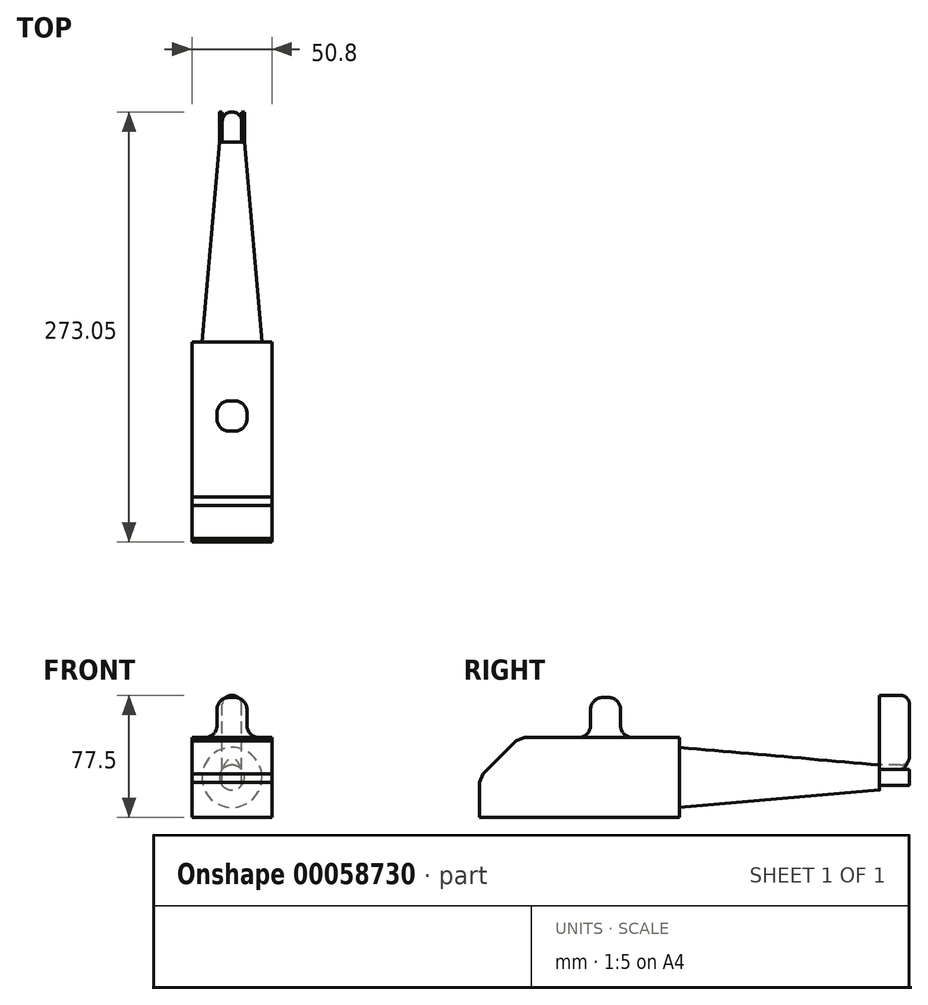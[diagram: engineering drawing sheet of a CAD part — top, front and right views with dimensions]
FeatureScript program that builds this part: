
annotation { "Feature Type Name" : "Feature", "Feature Type Description" : "" }
export const myFeature = defineFeature(function(context is Context, id is Id, definition is map)
    precondition{}
    {
        {
            var Q0;
            Q0=qCreatedBy(makeId("Top.planeOp"),FACE);
            var sketch = newSketch(context, id + "F0", { "sketchPlane" : qUnion([Q0])});
            skLineSegment(sketch, "E0.rect.bottom", {"start": v(25.4, -63.5) * mm, "end": v(-25.4, -63.5) * mm});
            skLineSegment(sketch, "E0.rect.top", {"start": v(25.4, 63.5) * mm, "end": v(-25.4, 63.5) * mm});
            skLineSegment(sketch, "E0.rect.left", {"start": v(25.4, -63.5) * mm, "end": v(25.4, 63.5) * mm});
            skLineSegment(sketch, "E0.rect.right", {"start": v(-25.4, -63.5) * mm, "end": v(-25.4, 63.5) * mm});
            skPoint(sketch, "E0.rect.middle", {"position": v(0, 0) * mm});
            skSolve(sketch);
        }
        {
            var Q0;
            Q0=makeQuery(id+"F0.imprint","IMPRINT",FACE,{"disambiguationData":[TD([[makeQuery(id+"F0.imprint","IMPRINT",EDGE,{"derivedFrom":sQuery(id+"F0.wireOp",EDGE,"E0.rect.bottom")}),-1.0]])]});
            extrude(context, id + "F1", {"entities" : qUnion([Q0]), "depth" : 50.8 * mm});
        }
        {
            var Q0;
            Q0=makeQuery(id+"F1.opExtrude","CAP_EDGE",EDGE,{"disambiguationData":[OSD([sQuery(id+"F0.wireOp",EDGE,"E0.rect.bottom")])],"isStart":false});
            chamfer(context, id + "F2", {"entities" : qUnion([Q0]), "width" : 25.4 * mm, "tangentPropagation" : true});
        }
        {
            var Q0;
            {var subQ0=sQuery(id+"F0.wireOp",EDGE,"E0.rect.bottom");Q0=makeQuery(id+"F2.opChamfer","BLEND_EDGE",EDGE,{"blendedFrom":[makeQuery(id+"F1.opExtrude","CAP_EDGE",EDGE,{"disambiguationData":[OSD([subQ0])],"isStart":false}),makeQuery(id+"F1.opExtrude","CAP_FACE",FACE,{"disambiguationData":[OSD([subQ0,sQuery(id+"F0.wireOp",EDGE,"E0.rect.top"),sQuery(id+"F0.wireOp",EDGE,"E0.rect.left"),sQuery(id+"F0.wireOp",EDGE,"E0.rect.right")])],"isStart":false})],"blendedInto":[makeQuery(id+"F1.opExtrude","CAP_FACE",FACE,{"disambiguationData":[OSD([subQ0,sQuery(id+"F0.wireOp",EDGE,"E0.rect.top"),sQuery(id+"F0.wireOp",EDGE,"E0.rect.left"),sQuery(id+"F0.wireOp",EDGE,"E0.rect.right")])],"isStart":false})]});}
            chamfer(context, id + "F3", {"entities" : qUnion([Q0]), "width" : 7.62 * mm, "tangentPropagation" : true});
        }
        {
            var Q0;
            {var subQ0=sQuery(id+"F0.wireOp",EDGE,"E0.rect.bottom");Q0=makeQuery(id+"F2.opChamfer","BLEND_EDGE",EDGE,{"blendedFrom":[makeQuery(id+"F1.opExtrude","CAP_EDGE",EDGE,{"disambiguationData":[OSD([subQ0])],"isStart":false}),makeQuery(id+"F1.opExtrude","SWEPT_FACE",FACE,{"disambiguationData":[OSD([subQ0])]})],"blendedInto":[makeQuery(id+"F1.opExtrude","SWEPT_FACE",FACE,{"disambiguationData":[OSD([subQ0])]})]});}
            chamfer(context, id + "F4", {"entities" : qUnion([Q0]), "width" : 7.62 * mm, "tangentPropagation" : true});
        }
        {
            var Q0;
            Q0=makeQuery(id+"F1.opExtrude","SWEPT_FACE",FACE,{"disambiguationData":[OSD([sQuery(id+"F0.wireOp",EDGE,"E0.rect.top")])]});
            var sketch = newSketch(context, id + "F5", { "sketchPlane" : qUnion([Q0])});
            skLineSegment(sketch, "E1", {"start": v(-25.4, 0) * mm, "end": v(25.4, 50.8) * mm});
            skLineSegment(sketch, "E2", {"start": v(25.4, 50.8) * mm, "end": v(-25.4, 50.8) * mm});
            skLineSegment(sketch, "E3", {"start": v(-25.4, 50.8) * mm, "end": v(25.4, 0) * mm});
            skCircle(sketch, "E4", {"center": v(0, 25.4) * mm, "radius": 19.05 * mm});
            skSolve(sketch);
        }
        {
            var Q0;
            {var subQ0=sQuery(id+"F5.wireOp",EDGE,"E3");var subQ1=sQuery(id+"F5.wireOp",EDGE,"E1");var subQ2=makeQuery(id+"F5.imprint","INTERSECT",VERTEX,{"derivedFrom":[subQ1,subQ0]});Q0=makeQuery(id+"F5.imprint","IMPRINT",FACE,{"disambiguationData":[TD([[makeQuery(id+"F5.imprint","IMPRINT",EDGE,{"disambiguationData":[TD([[subQ2,-1.0]])],"derivedFrom":subQ1}),-1.0]])]});}
            var Q1;
            {var subQ0=sQuery(id+"F5.wireOp",EDGE,"E4");var subQ1=sQuery(id+"F5.wireOp",EDGE,"E1");var subQ2=makeQuery(id+"F5.imprint","INTERSECT",VERTEX,{"disambiguationData":[OD(0.0)],"derivedFrom":[subQ1,subQ0]});Q1=makeQuery(id+"F5.imprint","IMPRINT",FACE,{"disambiguationData":[TD([[makeQuery(id+"F5.imprint","IMPRINT",EDGE,{"disambiguationData":[TD([[subQ2,-1.0]])],"derivedFrom":subQ1}),1.0]])]});}
            var Q2;
            {var subQ0=sQuery(id+"F5.wireOp",EDGE,"E4");var subQ1=sQuery(id+"F5.wireOp",EDGE,"E1");var subQ2=makeQuery(id+"F5.imprint","INTERSECT",VERTEX,{"disambiguationData":[OD(0.0)],"derivedFrom":[subQ1,subQ0]});Q2=makeQuery(id+"F5.imprint","IMPRINT",FACE,{"disambiguationData":[TD([[makeQuery(id+"F5.imprint","IMPRINT",EDGE,{"disambiguationData":[TD([[subQ2,-1.0]])],"derivedFrom":subQ1}),-1.0]])]});}
            var Q3;
            {var subQ0=sQuery(id+"F5.wireOp",EDGE,"E3");var subQ1=sQuery(id+"F5.wireOp",EDGE,"E1");var subQ2=makeQuery(id+"F5.imprint","INTERSECT",VERTEX,{"derivedFrom":[subQ1,subQ0]});Q3=makeQuery(id+"F5.imprint","IMPRINT",FACE,{"disambiguationData":[TD([[makeQuery(id+"F5.imprint","IMPRINT",EDGE,{"disambiguationData":[TD([[subQ2,-1.0]])],"derivedFrom":subQ1}),1.0]])]});}
            extrude(context, id + "F6", {"entities" : qUnion([Q0, Q1, Q2, Q3]), "operationType" : NewBodyOperationType.ADD, "depth" : 127 * mm, "hasDraft" : true, "draftAngle" : 5 * degree, "draftPullDirection" : true});
        }
        {
            var Q0;
            Q0=makeQuery(id+"F6.opExtrude","CAP_FACE",FACE,{"disambiguationData":[OSD([sQuery(id+"F5.wireOp",EDGE,"E4")])],"isStart":false});
            var sketch = newSketch(context, id + "F7", { "sketchPlane" : qUnion([Q0])});
            skLineSegment(sketch, "E5", {"start": v(-6.13, 20.35) * mm, "end": v(6.13, 20.35) * mm});
            skLineSegment(sketch, "E6.top", {"start": v(-6.13, 77.5) * mm, "end": v(6.13, 77.5) * mm});
            skLineSegment(sketch, "E6.left", {"start": v(-6.13, 20.35) * mm, "end": v(-6.13, 77.5) * mm});
            skLineSegment(sketch, "E6.right", {"start": v(6.13, 20.35) * mm, "end": v(6.13, 77.5) * mm});
            skSolve(sketch);
        }
        {
            var Q0;
            {var subQ0=sQuery(id+"F7.wireOp",EDGE,"E6.top");Q0=makeQuery(id+"F7.imprint","IMPRINT",FACE,{"disambiguationData":[TD([[makeQuery(id+"F7.imprint","IMPRINT",EDGE,{"derivedFrom":subQ0}),-1.0]])]});}
            var Q1;
            {var subQ0=sQuery(id+"F7.wireOp",EDGE,"E5");Q1=makeQuery(id+"F7.imprint","IMPRINT",FACE,{"disambiguationData":[TD([[makeQuery(id+"F7.imprint","IMPRINT",EDGE,{"derivedFrom":subQ0}),-1.0]])]});}
            var Q2;
            {var subQ0=sQuery(id+"F7.wireOp",EDGE,"E6.left");var subQ1=makeQuery(id+"F6.opExtrude","CAP_EDGE",EDGE,{"disambiguationData":[OSD([sQuery(id+"F5.wireOp",EDGE,"E4")])],"isStart":false});var subQ3=makeQuery(id+"F7.imprint","INTERSECT",VERTEX,{"derivedFrom":[subQ1,subQ0]});Q2=makeQuery(id+"F7.imprint","IMPRINT",FACE,{"disambiguationData":[TD([[makeQuery(id+"F7.imprint","IMPRINT",EDGE,{"disambiguationData":[TD([[subQ3,1.0]])],"derivedFrom":subQ0}),1.0]])]});}
            var Q3;
            {var subQ0=sQuery(id+"F7.wireOp",EDGE,"E6.right");var subQ1=makeQuery(id+"F6.opExtrude","CAP_EDGE",EDGE,{"disambiguationData":[OSD([sQuery(id+"F5.wireOp",EDGE,"E4")])],"isStart":false});var subQ3=makeQuery(id+"F7.imprint","INTERSECT",VERTEX,{"derivedFrom":[subQ1,subQ0]});Q3=makeQuery(id+"F7.imprint","IMPRINT",FACE,{"disambiguationData":[TD([[makeQuery(id+"F7.imprint","IMPRINT",EDGE,{"disambiguationData":[TD([[subQ3,1.0]])],"derivedFrom":subQ0}),-1.0]])]});}
            var Q4;
            {var subQ0=sQuery(id+"F7.wireOp",EDGE,"E5");Q4=makeQuery(id+"F7.imprint","IMPRINT",FACE,{"disambiguationData":[TD([[makeQuery(id+"F7.imprint","IMPRINT",EDGE,{"derivedFrom":subQ0}),1.0]])]});}
            extrude(context, id + "F8", {"entities" : qUnion([Q0, Q1, Q2, Q3, Q4]), "operationType" : NewBodyOperationType.ADD, "depth" : 19.05 * mm});
        }
        {
            var Q0;
            Q0=makeQuery(id+"F8.opExtrude","CAP_FACE",FACE,{"disambiguationData":[OSD([sQuery(id+"F5.wireOp",EDGE,"E4"),sQuery(id+"F7.wireOp",EDGE,"E6.top"),sQuery(id+"F7.wireOp",EDGE,"E6.left"),sQuery(id+"F7.wireOp",EDGE,"E6.right")])],"isStart":false});
            var Q1;
            Q1=makeQuery(id+"F8.opExtrude","SWEPT_EDGE",EDGE,{"disambiguationData":[OSD([sQuery(id+"F7.wireOp",EDGE,"E6.top"),sQuery(id+"F7.wireOp",EDGE,"E6.left")])]});
            var Q2;
            Q2=makeQuery(id+"F8.opExtrude","SWEPT_EDGE",EDGE,{"disambiguationData":[OSD([sQuery(id+"F7.wireOp",EDGE,"E6.top"),sQuery(id+"F7.wireOp",EDGE,"E6.right")])]});
            fillet(context, id + "F9", {"entities" : qUnion([Q0, Q1, Q2]), "radius" : 5.7 * mm, "tangentPropagation" : true, "allowEdgeOverflow" : false});
        }
        {
            var Q0;
            Q0=makeQuery(id+"F1.opExtrude","CAP_FACE",FACE,{"disambiguationData":[OSD([sQuery(id+"F0.wireOp",EDGE,"E0.rect.bottom"),sQuery(id+"F0.wireOp",EDGE,"E0.rect.top"),sQuery(id+"F0.wireOp",EDGE,"E0.rect.left"),sQuery(id+"F0.wireOp",EDGE,"E0.rect.right")])],"isStart":false});
            var sketch = newSketch(context, id + "F10", { "sketchPlane" : qUnion([Q0])});
            skLineSegment(sketch, "E7", {"start": v(-25.4, 63.5) * mm, "end": v(25.4, -30.48) * mm});
            skLineSegment(sketch, "E8.rect.bottom", {"start": v(-9.53, 6.98) * mm, "end": v(9.53, 6.98) * mm});
            skLineSegment(sketch, "E8.rect.top", {"start": v(-9.53, 26.03) * mm, "end": v(9.52, 26.03) * mm});
            skLineSegment(sketch, "E8.rect.left", {"start": v(-9.53, 6.98) * mm, "end": v(-9.53, 26.03) * mm});
            skLineSegment(sketch, "E8.rect.right", {"start": v(9.53, 6.98) * mm, "end": v(9.52, 26.03) * mm});
            skPoint(sketch, "E8.rect.middle", {"position": v(0, 16.5) * mm});
            skSolve(sketch);
        }
        {
            var Q0;
            {var subQ5=sQuery(id+"F10.wireOp",EDGE,"E8.rect.left");Q0=makeQuery(id+"F10.imprint","IMPRINT",FACE,{"disambiguationData":[TD([[makeQuery(id+"F10.imprint","IMPRINT",EDGE,{"derivedFrom":subQ5}),-1.0]])]});}
            var Q1;
            {var subQ5=sQuery(id+"F10.wireOp",EDGE,"E8.rect.right");Q1=makeQuery(id+"F10.imprint","IMPRINT",FACE,{"disambiguationData":[TD([[makeQuery(id+"F10.imprint","IMPRINT",EDGE,{"derivedFrom":subQ5}),1.0]])]});}
            extrude(context, id + "F11", {"entities" : qUnion([Q0, Q1]), "operationType" : NewBodyOperationType.ADD, "depth" : 25.4 * mm});
        }
        {
            var Q0;
            Q0=makeQuery(id+"F11.opExtrude","SWEPT_FACE",FACE,{"disambiguationData":[OSD([sQuery(id+"F10.wireOp",EDGE,"E8.rect.top")])]});
            var Q1;
            Q1=makeQuery(id+"F11.opExtrude","SWEPT_FACE",FACE,{"disambiguationData":[OSD([sQuery(id+"F10.wireOp",EDGE,"E8.rect.left")])]});
            var Q2;
            Q2=makeQuery(id+"F11.opExtrude","SWEPT_FACE",FACE,{"disambiguationData":[OSD([sQuery(id+"F10.wireOp",EDGE,"E8.rect.bottom")])]});
            var Q3;
            Q3=makeQuery(id+"F11.opExtrude","SWEPT_FACE",FACE,{"disambiguationData":[OSD([sQuery(id+"F10.wireOp",EDGE,"E8.rect.right")])]});
            fillet(context, id + "F12", {"entities" : qUnion([Q0, Q1, Q2, Q3]), "radius" : 7.62 * mm, "tangentPropagation" : true, "allowEdgeOverflow" : false});
        }
    });
